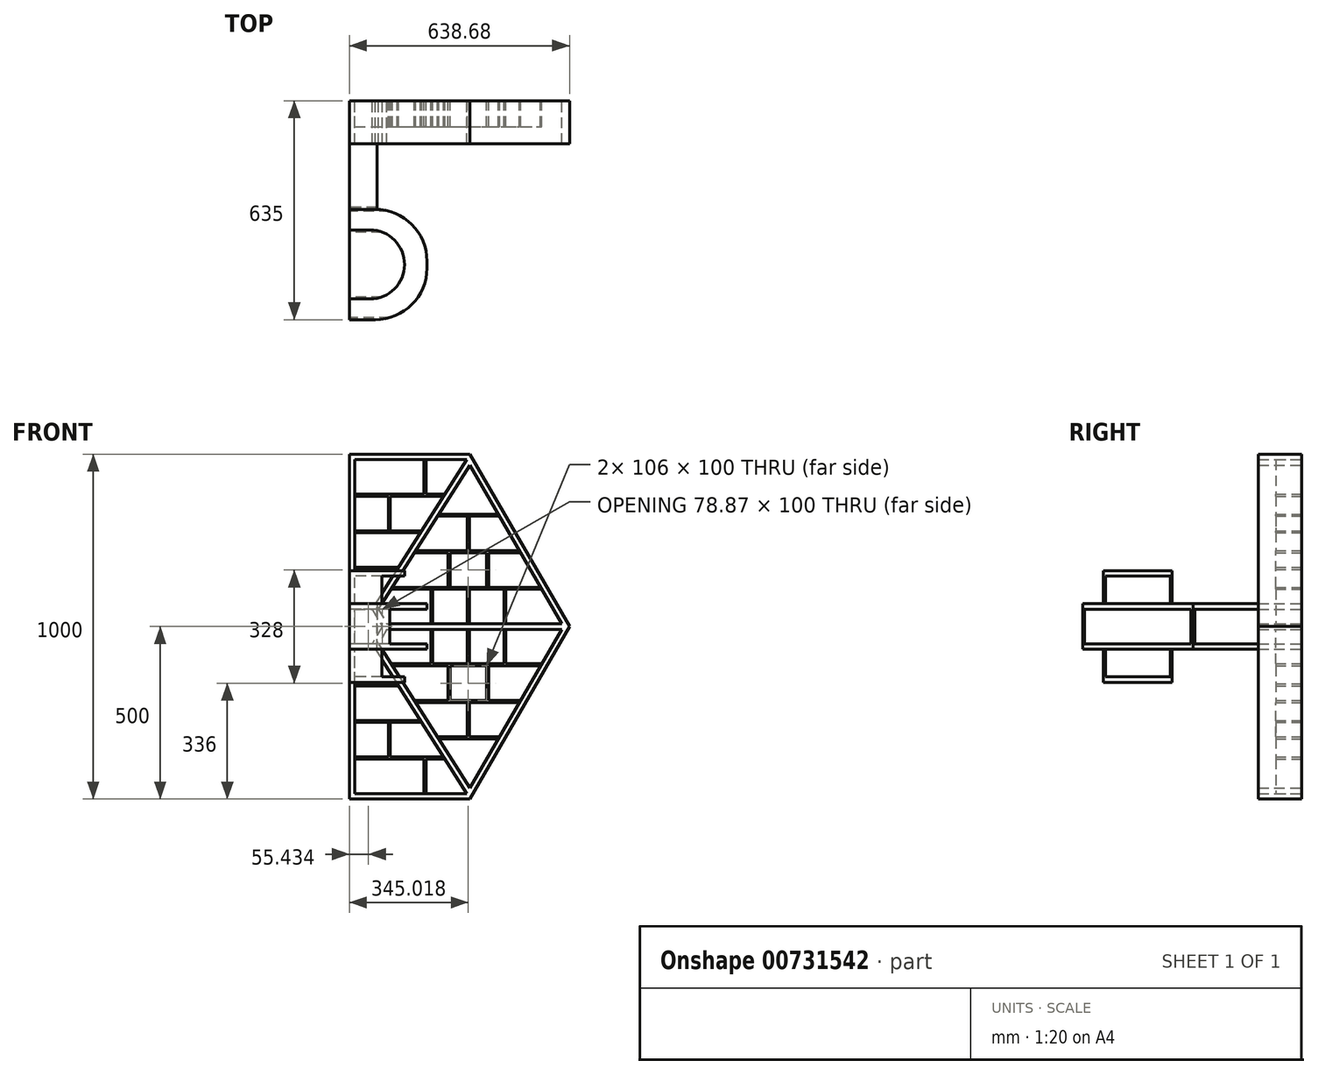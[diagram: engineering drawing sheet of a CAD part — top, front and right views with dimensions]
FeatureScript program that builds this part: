
annotation { "Feature Type Name" : "Feature", "Feature Type Description" : "" }
export const myFeature = defineFeature(function(context is Context, id is Id, definition is map)
    precondition{}
    {
        {
            var Q0;
            Q0=qCreatedBy(makeId("Front.planeOp"),FACE);
            var sketch = newSketch(context, id + "F0", { "sketchPlane" : qUnion([Q0])});
            skLineSegment(sketch, "E0", {"start": v(0, 0) * mm, "end": v(0, 1000) * mm, "construction": true});
            skLineSegment(sketch, "E1", {"start": v(0, 1000) * mm, "end": v(1200, 0) * mm, "construction": true});
            skLineSegment(sketch, "E2", {"start": v(1200, 0) * mm, "end": v(0, 0) * mm, "construction": true});
            skSolve(sketch);
        }
        {
            var Q0;
            Q0=qCreatedBy(makeId("Front.planeOp"),FACE);
            var sketch = newSketch(context, id + "F1", { "sketchPlane" : qUnion([Q0])});
            skLineSegment(sketch, "E3", {"start": v(0, 0) * mm, "end": v(350, 0) * mm});
            skLineSegment(sketch, "E4", {"start": v(350, 1000) * mm, "end": v(0, 1000) * mm});
            skLineSegment(sketch, "E5", {"start": v(0, 1000) * mm, "end": v(0, 0) * mm});
            skLineSegment(sketch, "E6", {"start": v(-31.63, 500) * mm, "end": v(1001.42, 500) * mm, "construction": true});
            skLineSegment(sketch, "E7", {"start": v(350, 1000) * mm, "end": v(638.68, 500) * mm});
            skLineSegment(sketch, "E8", {"start": v(638.68, 500) * mm, "end": v(350, 0) * mm});
            skLineSegment(sketch, "E9", {"start": v(16, 984) * mm, "end": v(340.76, 984) * mm});
            skLineSegment(sketch, "E10", {"start": v(340.76, 984) * mm, "end": v(620.2, 500) * mm});
            skLineSegment(sketch, "E11", {"start": v(620.2, 500) * mm, "end": v(340.76, 16) * mm});
            skLineSegment(sketch, "E12", {"start": v(340.76, 16) * mm, "end": v(16, 16) * mm});
            skLineSegment(sketch, "E13", {"start": v(16, 16) * mm, "end": v(16, 984) * mm});
            skLineSegment(sketch, "E14", {"start": v(16, 550) * mm, "end": v(66, 550) * mm});
            skLineSegment(sketch, "E15", {"start": v(66, 550) * mm, "end": v(94.87, 500) * mm});
            skLineSegment(sketch, "E16", {"start": v(94.87, 500) * mm, "end": v(66, 450) * mm});
            skLineSegment(sketch, "E17", {"start": v(66, 450) * mm, "end": v(16, 450) * mm});
            skLineSegment(sketch, "E18", {"start": v(16, 450) * mm, "end": v(16, 550) * mm});
            skLineSegment(sketch, "E19.0", {"start": v(75.24, 434) * mm, "end": v(16, 434) * mm});
            skLineSegment(sketch, "E19.1", {"start": v(113.34, 500) * mm, "end": v(75.24, 434) * mm});
            skLineSegment(sketch, "E19.2", {"start": v(75.24, 566) * mm, "end": v(113.34, 500) * mm});
            skLineSegment(sketch, "E19.3", {"start": v(16, 566) * mm, "end": v(75.24, 566) * mm});
            skLineSegment(sketch, "E20", {"start": v(340.76, 984) * mm, "end": v(75.24, 566) * mm});
            skLineSegment(sketch, "E21", {"start": v(75.24, 434) * mm, "end": v(340.76, 16) * mm});
            skLineSegment(sketch, "E22", {"start": v(113.34, 500) * mm, "end": v(620.2, 500) * mm, "construction": true});
            skLineSegment(sketch, "E23", {"start": v(84.26, 449.63) * mm, "end": v(349.79, 31.63) * mm});
            skLineSegment(sketch, "E24", {"start": v(84.26, 550.37) * mm, "end": v(349.79, 968.37) * mm});
            skLineSegment(sketch, "E25", {"start": v(108.72, 508) * mm, "end": v(615.58, 508) * mm});
            skLineSegment(sketch, "E26", {"start": v(108.72, 492) * mm, "end": v(615.58, 492) * mm});
            skLineSegment(sketch, "E27", {"start": v(120.87, 608) * mm, "end": v(557.85, 608) * mm});
            skLineSegment(sketch, "E28", {"start": v(124.68, 614) * mm, "end": v(554.38, 614) * mm});
            skLineSegment(sketch, "E29", {"start": v(188.2, 714) * mm, "end": v(496.65, 714) * mm});
            skLineSegment(sketch, "E30", {"start": v(192.02, 720) * mm, "end": v(493.18, 720) * mm});
            skLineSegment(sketch, "E31", {"start": v(255.54, 820) * mm, "end": v(435.45, 820) * mm});
            skLineSegment(sketch, "E32", {"start": v(259.35, 826) * mm, "end": v(431.98, 826) * mm});
            skLineSegment(sketch, "E33", {"start": v(16, 884) * mm, "end": v(277.24, 884) * mm});
            skLineSegment(sketch, "E34", {"start": v(16, 878) * mm, "end": v(273.43, 878) * mm});
            skLineSegment(sketch, "E35", {"start": v(16, 778) * mm, "end": v(209.9, 778) * mm});
            skLineSegment(sketch, "E36", {"start": v(16, 772) * mm, "end": v(206.1, 772) * mm});
            skLineSegment(sketch, "E37", {"start": v(16, 672) * mm, "end": v(142.57, 672) * mm});
            skLineSegment(sketch, "E38", {"start": v(16, 666) * mm, "end": v(138.76, 666) * mm});
            skLineSegment(sketch, "E39.MirrorCS", {"start": v(120.87, 392) * mm, "end": v(557.85, 392) * mm});
            skLineSegment(sketch, "E40.MirrorCS", {"start": v(124.68, 386) * mm, "end": v(554.38, 386) * mm});
            skLineSegment(sketch, "E41.MirrorCS", {"start": v(188.2, 286) * mm, "end": v(496.65, 286) * mm});
            skLineSegment(sketch, "E42.MirrorCS", {"start": v(192.02, 280) * mm, "end": v(493.18, 280) * mm});
            skLineSegment(sketch, "E43.MirrorCS", {"start": v(255.54, 180) * mm, "end": v(435.45, 180) * mm});
            skLineSegment(sketch, "E44.MirrorCS", {"start": v(259.35, 174) * mm, "end": v(431.98, 174) * mm});
            skLineSegment(sketch, "E45.MirrorCS", {"start": v(16, 116) * mm, "end": v(277.24, 116) * mm});
            skLineSegment(sketch, "E46.MirrorCS", {"start": v(16, 122) * mm, "end": v(273.43, 122) * mm});
            skLineSegment(sketch, "E47.MirrorCS", {"start": v(16, 222) * mm, "end": v(209.9, 222) * mm});
            skLineSegment(sketch, "E48.MirrorCS", {"start": v(16, 228) * mm, "end": v(206.1, 228) * mm});
            skLineSegment(sketch, "E49.MirrorCS", {"start": v(16, 328) * mm, "end": v(142.57, 328) * mm});
            skLineSegment(sketch, "E50.MirrorCS", {"start": v(16, 334) * mm, "end": v(138.76, 334) * mm});
            skLineSegment(sketch, "E51", {"start": v(112.95, 778) * mm, "end": v(112.95, 878) * mm});
            skLineSegment(sketch, "E52", {"start": v(118.95, 878) * mm, "end": v(118.95, 778) * mm});
            skLineSegment(sketch, "E53", {"start": v(216, 884) * mm, "end": v(216, 984) * mm});
            skLineSegment(sketch, "E54", {"start": v(222, 984) * mm, "end": v(222, 884) * mm});
            skLineSegment(sketch, "E55.MirrorCS", {"start": v(112.95, 222) * mm, "end": v(112.95, 122) * mm});
            skLineSegment(sketch, "E56.MirrorCS", {"start": v(118.95, 122) * mm, "end": v(118.95, 222) * mm});
            skLineSegment(sketch, "E57.MirrorCS", {"start": v(216, 116) * mm, "end": v(216, 16) * mm});
            skLineSegment(sketch, "E58.MirrorCS", {"start": v(222, 16) * mm, "end": v(222, 116) * mm});
            skLineSegment(sketch, "E59", {"start": v(342.02, 820) * mm, "end": v(342.02, 720) * mm});
            skLineSegment(sketch, "E60", {"start": v(348.02, 820) * mm, "end": v(348.02, 720) * mm});
            skLineSegment(sketch, "E61", {"start": v(292.02, 714) * mm, "end": v(292.02, 614) * mm});
            skLineSegment(sketch, "E62", {"start": v(286.02, 614) * mm, "end": v(292.02, 614) * mm});
            skLineSegment(sketch, "E63", {"start": v(286.02, 614) * mm, "end": v(286.02, 714) * mm});
            skLineSegment(sketch, "E64", {"start": v(404.02, 714) * mm, "end": v(404.02, 614) * mm});
            skLineSegment(sketch, "E65", {"start": v(404.02, 614) * mm, "end": v(398.02, 614) * mm});
            skLineSegment(sketch, "E66", {"start": v(398.02, 614) * mm, "end": v(398.02, 714) * mm});
            skLineSegment(sketch, "E67", {"start": v(342.02, 608) * mm, "end": v(342.02, 508) * mm});
            skLineSegment(sketch, "E68", {"start": v(342.02, 508) * mm, "end": v(348.02, 508) * mm});
            skLineSegment(sketch, "E69", {"start": v(348.02, 508) * mm, "end": v(348.02, 608) * mm});
            skLineSegment(sketch, "E70", {"start": v(448.02, 508) * mm, "end": v(448.02, 608) * mm});
            skLineSegment(sketch, "E71", {"start": v(448.02, 608) * mm, "end": v(454.02, 608) * mm});
            skLineSegment(sketch, "E72", {"start": v(454.02, 608) * mm, "end": v(454.02, 508) * mm});
            skLineSegment(sketch, "E73", {"start": v(242.02, 608) * mm, "end": v(242.02, 508) * mm});
            skLineSegment(sketch, "E74", {"start": v(236.02, 608) * mm, "end": v(236.02, 508) * mm});
            skLineSegment(sketch, "E75.MirrorCS", {"start": v(342.02, 180) * mm, "end": v(342.02, 280) * mm});
            skLineSegment(sketch, "E76.MirrorCS", {"start": v(348.02, 180) * mm, "end": v(348.02, 280) * mm});
            skLineSegment(sketch, "E77.MirrorCS", {"start": v(404.02, 286) * mm, "end": v(404.02, 386) * mm});
            skLineSegment(sketch, "E78.MirrorCS", {"start": v(398.02, 386) * mm, "end": v(398.02, 286) * mm});
            skLineSegment(sketch, "E79.MirrorCS", {"start": v(292.02, 286) * mm, "end": v(292.02, 386) * mm});
            skLineSegment(sketch, "E80.MirrorCS", {"start": v(286.02, 386) * mm, "end": v(286.02, 286) * mm});
            skLineSegment(sketch, "E81.MirrorCS", {"start": v(236.02, 392) * mm, "end": v(236.02, 492) * mm});
            skLineSegment(sketch, "E82.MirrorCS", {"start": v(242.02, 392) * mm, "end": v(242.02, 492) * mm});
            skLineSegment(sketch, "E83.MirrorCS", {"start": v(342.02, 392) * mm, "end": v(342.02, 492) * mm});
            skLineSegment(sketch, "E84.MirrorCS", {"start": v(348.02, 492) * mm, "end": v(348.02, 392) * mm});
            skLineSegment(sketch, "E85.MirrorCS", {"start": v(448.02, 492) * mm, "end": v(448.02, 392) * mm});
            skLineSegment(sketch, "E86.MirrorCS", {"start": v(454.02, 392) * mm, "end": v(454.02, 492) * mm});
            skSolve(sketch);
        }
        {
            var Q0;
            {var subQ4=sQuery(id+"F1.wireOp",EDGE,"E21");var subQ9=makeQuery(id+"F1.imprint","INTERSECT",VERTEX,{"derivedFrom":[subQ4,sQuery(id+"F1.wireOp",EDGE,"E46.MirrorCS")]});Q0=makeQuery(id+"F1.imprint","IMPRINT",FACE,{"disambiguationData":[TD([[makeQuery(id+"F1.imprint","IMPRINT",EDGE,{"disambiguationData":[TD([[subQ9,1.0]])],"derivedFrom":subQ4}),1.0]])]});}
            var Q1;
            {var subQ7=sQuery(id+"F1.wireOp",EDGE,"E14");Q1=makeQuery(id+"F1.imprint","IMPRINT",FACE,{"disambiguationData":[TD([[makeQuery(id+"F1.imprint","IMPRINT",EDGE,{"derivedFrom":subQ7}),1.0]])]});}
            var Q2;
            Q2=makeQuery(id+"F1.imprint","IMPRINT",FACE,{"disambiguationData":[TD([[makeQuery(id+"F1.imprint","IMPRINT",EDGE,{"derivedFrom":sQuery(id+"F1.wireOp",EDGE,"E3")}),1.0]])]});
            var Q3;
            {var subQ4=sQuery(id+"F1.wireOp",EDGE,"E20");var subQ5=makeQuery(id+"F1.imprint","INTERSECT",VERTEX,{"derivedFrom":[subQ4,sQuery(id+"F1.wireOp",EDGE,"E36")]});Q3=makeQuery(id+"F1.imprint","IMPRINT",FACE,{"disambiguationData":[TD([[makeQuery(id+"F1.imprint","IMPRINT",EDGE,{"disambiguationData":[TD([[subQ5,-1.0]])],"derivedFrom":subQ4}),1.0]])]});}
            var Q4;
            {var subQ3=sQuery(id+"F1.wireOp",EDGE,"E11");var subQ4=sQuery(id+"F1.wireOp",EDGE,"E10");var subQ5=makeQuery(id+"F1.imprint","INTERSECT",VERTEX,{"derivedFrom":[subQ4,subQ3]});Q4=makeQuery(id+"F1.imprint","IMPRINT",FACE,{"disambiguationData":[TD([[makeQuery(id+"F1.imprint","IMPRINT",EDGE,{"disambiguationData":[TD([[subQ5,1.0]])],"derivedFrom":subQ4}),-1.0]])]});}
            extrude(context, id + "F2", {"entities" : qUnion([Q0, Q1, Q2, Q3, Q4]), "depth" : 125 * mm, "offsetDistance" : 25 * mm});
        }
        {
            var Q0;
            {var subQ0=sQuery(id+"F1.wireOp",EDGE,"E45.MirrorCS");var subQ4=sQuery(id+"F1.wireOp",EDGE,"E13");var subQ5=makeQuery(id+"F1.imprint","INTERSECT",VERTEX,{"derivedFrom":[subQ4,subQ0]});Q0=makeQuery(id+"F1.imprint","IMPRINT",FACE,{"disambiguationData":[TD([[makeQuery(id+"F1.imprint","IMPRINT",EDGE,{"disambiguationData":[TD([[subQ5,-1.0]])],"derivedFrom":subQ4}),-1.0]])]});}
            var Q1;
            {var subQ0=sQuery(id+"F1.wireOp",EDGE,"E57.MirrorCS");Q1=makeQuery(id+"F1.imprint","IMPRINT",FACE,{"disambiguationData":[TD([[makeQuery(id+"F1.imprint","IMPRINT",EDGE,{"derivedFrom":subQ0}),1.0]])]});}
            var Q2;
            {var subQ2=sQuery(id+"F1.wireOp",EDGE,"E55.MirrorCS");Q2=makeQuery(id+"F1.imprint","IMPRINT",FACE,{"disambiguationData":[TD([[makeQuery(id+"F1.imprint","IMPRINT",EDGE,{"derivedFrom":subQ2}),1.0]])]});}
            var Q3;
            {var subQ7=sQuery(id+"F1.wireOp",EDGE,"E48.MirrorCS");Q3=makeQuery(id+"F1.imprint","IMPRINT",FACE,{"disambiguationData":[TD([[makeQuery(id+"F1.imprint","IMPRINT",EDGE,{"derivedFrom":subQ7}),-1.0]])]});}
            var Q4;
            {var subQ2=sQuery(id+"F1.wireOp",EDGE,"E49.MirrorCS");Q4=makeQuery(id+"F1.imprint","IMPRINT",FACE,{"disambiguationData":[TD([[makeQuery(id+"F1.imprint","IMPRINT",EDGE,{"derivedFrom":subQ2}),1.0]])]});}
            var Q5;
            {var subQ7=sQuery(id+"F1.wireOp",EDGE,"E44.MirrorCS");Q5=makeQuery(id+"F1.imprint","IMPRINT",FACE,{"disambiguationData":[TD([[makeQuery(id+"F1.imprint","IMPRINT",EDGE,{"derivedFrom":subQ7}),1.0]])]});}
            var Q6;
            {var subQ2=sQuery(id+"F1.wireOp",EDGE,"E75.MirrorCS");Q6=makeQuery(id+"F1.imprint","IMPRINT",FACE,{"disambiguationData":[TD([[makeQuery(id+"F1.imprint","IMPRINT",EDGE,{"derivedFrom":subQ2}),-1.0]])]});}
            var Q7;
            {var subQ6=sQuery(id+"F1.wireOp",EDGE,"E42.MirrorCS");var subQ8=sQuery(id+"F1.wireOp",EDGE,"E11");var subQ9=makeQuery(id+"F1.imprint","INTERSECT",VERTEX,{"derivedFrom":[subQ8,subQ6]});Q7=makeQuery(id+"F1.imprint","IMPRINT",FACE,{"disambiguationData":[TD([[makeQuery(id+"F1.imprint","IMPRINT",EDGE,{"disambiguationData":[TD([[subQ9,1.0]])],"derivedFrom":subQ8}),-1.0]])]});}
            var Q8;
            {var subQ0=sQuery(id+"F1.wireOp",EDGE,"E79.MirrorCS");Q8=makeQuery(id+"F1.imprint","IMPRINT",FACE,{"disambiguationData":[TD([[makeQuery(id+"F1.imprint","IMPRINT",EDGE,{"derivedFrom":subQ0}),1.0]])]});}
            var Q9;
            {var subQ0=sQuery(id+"F1.wireOp",EDGE,"E77.MirrorCS");Q9=makeQuery(id+"F1.imprint","IMPRINT",FACE,{"disambiguationData":[TD([[makeQuery(id+"F1.imprint","IMPRINT",EDGE,{"derivedFrom":subQ0}),1.0]])]});}
            var Q10;
            {var subQ0=sQuery(id+"F1.wireOp",EDGE,"E40.MirrorCS");var subQ11=sQuery(id+"F1.wireOp",EDGE,"E11");var subQ12=makeQuery(id+"F1.imprint","INTERSECT",VERTEX,{"derivedFrom":[subQ11,subQ0]});Q10=makeQuery(id+"F1.imprint","IMPRINT",FACE,{"disambiguationData":[TD([[makeQuery(id+"F1.imprint","IMPRINT",EDGE,{"disambiguationData":[TD([[subQ12,1.0]])],"derivedFrom":subQ11}),-1.0]])]});}
            var Q11;
            {var subQ2=sQuery(id+"F1.wireOp",EDGE,"E83.MirrorCS");Q11=makeQuery(id+"F1.imprint","IMPRINT",FACE,{"disambiguationData":[TD([[makeQuery(id+"F1.imprint","IMPRINT",EDGE,{"derivedFrom":subQ2}),-1.0]])]});}
            var Q12;
            {var subQ0=sQuery(id+"F1.wireOp",EDGE,"E81.MirrorCS");Q12=makeQuery(id+"F1.imprint","IMPRINT",FACE,{"disambiguationData":[TD([[makeQuery(id+"F1.imprint","IMPRINT",EDGE,{"derivedFrom":subQ0}),-1.0]])]});}
            var Q13;
            {var subQ2=sQuery(id+"F1.wireOp",EDGE,"E85.MirrorCS");Q13=makeQuery(id+"F1.imprint","IMPRINT",FACE,{"disambiguationData":[TD([[makeQuery(id+"F1.imprint","IMPRINT",EDGE,{"derivedFrom":subQ2}),1.0]])]});}
            var Q14;
            {var subQ0=sQuery(id+"F1.wireOp",EDGE,"E64");Q14=makeQuery(id+"F1.imprint","IMPRINT",FACE,{"disambiguationData":[TD([[makeQuery(id+"F1.imprint","IMPRINT",EDGE,{"derivedFrom":subQ0}),-1.0]])]});}
            var Q15;
            {var subQ0=sQuery(id+"F1.wireOp",EDGE,"E29");var subQ9=sQuery(id+"F1.wireOp",EDGE,"E10");var subQ11=makeQuery(id+"F1.imprint","INTERSECT",VERTEX,{"derivedFrom":[subQ9,subQ0]});Q15=makeQuery(id+"F1.imprint","IMPRINT",FACE,{"disambiguationData":[TD([[makeQuery(id+"F1.imprint","IMPRINT",EDGE,{"disambiguationData":[TD([[subQ11,1.0]])],"derivedFrom":subQ9}),-1.0]])]});}
            var Q16;
            {var subQ2=sQuery(id+"F1.wireOp",EDGE,"E59");Q16=makeQuery(id+"F1.imprint","IMPRINT",FACE,{"disambiguationData":[TD([[makeQuery(id+"F1.imprint","IMPRINT",EDGE,{"derivedFrom":subQ2}),1.0]])]});}
            var Q17;
            {var subQ0=sQuery(id+"F1.wireOp",EDGE,"E28");var subQ12=sQuery(id+"F1.wireOp",EDGE,"E10");var subQ13=makeQuery(id+"F1.imprint","INTERSECT",VERTEX,{"derivedFrom":[subQ12,subQ0]});Q17=makeQuery(id+"F1.imprint","IMPRINT",FACE,{"disambiguationData":[TD([[makeQuery(id+"F1.imprint","IMPRINT",EDGE,{"disambiguationData":[TD([[subQ13,-1.0]])],"derivedFrom":subQ12}),-1.0]])]});}
            var Q18;
            {var subQ2=sQuery(id+"F1.wireOp",EDGE,"E70");Q18=makeQuery(id+"F1.imprint","IMPRINT",FACE,{"disambiguationData":[TD([[makeQuery(id+"F1.imprint","IMPRINT",EDGE,{"derivedFrom":subQ2}),-1.0]])]});}
            var Q19;
            {var subQ0=sQuery(id+"F1.wireOp",EDGE,"E73");Q19=makeQuery(id+"F1.imprint","IMPRINT",FACE,{"disambiguationData":[TD([[makeQuery(id+"F1.imprint","IMPRINT",EDGE,{"derivedFrom":subQ0}),-1.0]])]});}
            var Q20;
            {var subQ2=sQuery(id+"F1.wireOp",EDGE,"E67");Q20=makeQuery(id+"F1.imprint","IMPRINT",FACE,{"disambiguationData":[TD([[makeQuery(id+"F1.imprint","IMPRINT",EDGE,{"derivedFrom":subQ2}),1.0]])]});}
            var Q21;
            {var subQ0=sQuery(id+"F1.wireOp",EDGE,"E37");Q21=makeQuery(id+"F1.imprint","IMPRINT",FACE,{"disambiguationData":[TD([[makeQuery(id+"F1.imprint","IMPRINT",EDGE,{"derivedFrom":subQ0}),-1.0]])]});}
            var Q22;
            {var subQ4=sQuery(id+"F1.wireOp",EDGE,"E36");Q22=makeQuery(id+"F1.imprint","IMPRINT",FACE,{"disambiguationData":[TD([[makeQuery(id+"F1.imprint","IMPRINT",EDGE,{"derivedFrom":subQ4}),1.0]])]});}
            var Q23;
            {var subQ2=sQuery(id+"F1.wireOp",EDGE,"E51");Q23=makeQuery(id+"F1.imprint","IMPRINT",FACE,{"disambiguationData":[TD([[makeQuery(id+"F1.imprint","IMPRINT",EDGE,{"derivedFrom":subQ2}),-1.0]])]});}
            var Q24;
            {var subQ0=sQuery(id+"F1.wireOp",EDGE,"E33");var subQ4=sQuery(id+"F1.wireOp",EDGE,"E13");var subQ5=makeQuery(id+"F1.imprint","INTERSECT",VERTEX,{"derivedFrom":[subQ4,subQ0]});Q24=makeQuery(id+"F1.imprint","IMPRINT",FACE,{"disambiguationData":[TD([[makeQuery(id+"F1.imprint","IMPRINT",EDGE,{"disambiguationData":[TD([[subQ5,1.0]])],"derivedFrom":subQ4}),-1.0]])]});}
            var Q25;
            {var subQ2=sQuery(id+"F1.wireOp",EDGE,"E53");Q25=makeQuery(id+"F1.imprint","IMPRINT",FACE,{"disambiguationData":[TD([[makeQuery(id+"F1.imprint","IMPRINT",EDGE,{"derivedFrom":subQ2}),-1.0]])]});}
            var Q26;
            {var subQ4=sQuery(id+"F1.wireOp",EDGE,"E32");Q26=makeQuery(id+"F1.imprint","IMPRINT",FACE,{"disambiguationData":[TD([[makeQuery(id+"F1.imprint","IMPRINT",EDGE,{"derivedFrom":subQ4}),-1.0]])]});}
            var Q27;
            {var subQ0=sQuery(id+"F1.wireOp",EDGE,"E61");Q27=makeQuery(id+"F1.imprint","IMPRINT",FACE,{"disambiguationData":[TD([[makeQuery(id+"F1.imprint","IMPRINT",EDGE,{"derivedFrom":subQ0}),-1.0]])]});}
            extrude(context, id + "F3", {"entities" : qUnion([Q0, Q1, Q2, Q3, Q4, Q5, Q6, Q7, Q8, Q9, Q10, Q11, Q12, Q13, Q14, Q15, Q16, Q17, Q18, Q19, Q20, Q21, Q22, Q23, Q24, Q25, Q26, Q27]), "operationType" : NewBodyOperationType.ADD, "depth" : 75 * mm, "offsetDistance" : 25 * mm});
        }
        {
            var Q0;
            Q0=qCreatedBy(makeId("Right.planeOp"),FACE);
            var sketch = newSketch(context, id + "F4", { "sketchPlane" : qUnion([Q0])});
            skLineSegment(sketch, "E87", {"start": v(0, 0) * mm, "end": v(0, 951) * mm, "construction": true});
            skLineSegment(sketch, "E88", {"start": v(-125, 0) * mm, "end": v(-125, 1000) * mm, "construction": true});
            skLineSegment(sketch, "E89", {"start": v(-125, 500) * mm, "end": v(-825, 500) * mm, "construction": true});
            skLineSegment(sketch, "E90", {"start": v(-125, 550) * mm, "end": v(-825, 550) * mm});
            skLineSegment(sketch, "E91", {"start": v(-825, 550) * mm, "end": v(-825, 450) * mm, "construction": true});
            skLineSegment(sketch, "E92", {"start": v(-825, 450) * mm, "end": v(-125, 450) * mm});
            skLineSegment(sketch, "E93", {"start": v(-125, 566) * mm, "end": v(-825, 566) * mm});
            skLineSegment(sketch, "E94", {"start": v(-825, 566) * mm, "end": v(-825, 550) * mm});
            skLineSegment(sketch, "E95", {"start": v(-475, 500) * mm, "end": v(-475, 885.02) * mm, "construction": true});
            skLineSegment(sketch, "E96", {"start": v(-575, 646) * mm, "end": v(-375, 646) * mm});
            skLineSegment(sketch, "E97", {"start": v(-575, 662) * mm, "end": v(-375, 662) * mm});
            skLineSegment(sketch, "E98", {"start": v(-575, 662) * mm, "end": v(-575, 646) * mm});
            skLineSegment(sketch, "E99", {"start": v(-375, 662) * mm, "end": v(-375, 646) * mm});
            skLineSegment(sketch, "E100", {"start": v(-575, 646) * mm, "end": v(-575, 566) * mm});
            skLineSegment(sketch, "E101", {"start": v(-569, 646) * mm, "end": v(-569, 566) * mm});
            skLineSegment(sketch, "E102", {"start": v(-375, 646) * mm, "end": v(-375, 566) * mm});
            skLineSegment(sketch, "E103", {"start": v(-381, 646) * mm, "end": v(-381, 566) * mm});
            skLineSegment(sketch, "E104", {"start": v(-125, 566) * mm, "end": v(-125, 550) * mm});
            skCircle(sketch, "E105", {"center": v(-475, 500) * mm, "radius": 173.37 * mm, "construction": true});
            skLineSegment(sketch, "E106.MirrorCS", {"start": v(-125, 450) * mm, "end": v(-825, 450) * mm});
            skLineSegment(sketch, "E107.MirrorCS", {"start": v(-125, 434) * mm, "end": v(-825, 434) * mm});
            skLineSegment(sketch, "E108.MirrorCS", {"start": v(-825, 434) * mm, "end": v(-825, 450) * mm});
            skLineSegment(sketch, "E109.MirrorCS", {"start": v(-125, 434) * mm, "end": v(-125, 450) * mm});
            skLineSegment(sketch, "E110.MirrorCS", {"start": v(-381, 354) * mm, "end": v(-381, 434) * mm});
            skLineSegment(sketch, "E111.MirrorCS", {"start": v(-375, 354) * mm, "end": v(-375, 434) * mm});
            skLineSegment(sketch, "E112.MirrorCS", {"start": v(-575, 354) * mm, "end": v(-375, 354) * mm});
            skLineSegment(sketch, "E113.MirrorCS", {"start": v(-375, 338) * mm, "end": v(-375, 354) * mm});
            skLineSegment(sketch, "E114.MirrorCS", {"start": v(-575, 338) * mm, "end": v(-375, 338) * mm});
            skLineSegment(sketch, "E115.MirrorCS", {"start": v(-575, 354) * mm, "end": v(-575, 434) * mm});
            skLineSegment(sketch, "E116.MirrorCS", {"start": v(-569, 354) * mm, "end": v(-569, 434) * mm});
            skLineSegment(sketch, "E117.MirrorCS", {"start": v(-575, 338) * mm, "end": v(-575, 354) * mm});
            skLineSegment(sketch, "E118", {"start": v(-825, 550) * mm, "end": v(-825, 450) * mm});
            skLineSegment(sketch, "E119", {"start": v(-819, 550) * mm, "end": v(-819, 450) * mm});
            skLineSegment(sketch, "E120", {"start": v(-635, 550) * mm, "end": v(-635, 450) * mm});
            skLineSegment(sketch, "E121", {"start": v(-635, 450) * mm, "end": v(-641, 450) * mm});
            skLineSegment(sketch, "E122", {"start": v(-641, 450) * mm, "end": v(-641, 550) * mm});
            skLineSegment(sketch, "E123", {"start": v(-641, 550) * mm, "end": v(-635, 550) * mm});
            skLineSegment(sketch, "E124", {"start": v(-309, 550) * mm, "end": v(-309, 450) * mm});
            skLineSegment(sketch, "E125", {"start": v(-309, 450) * mm, "end": v(-315, 450) * mm});
            skLineSegment(sketch, "E126", {"start": v(-315, 450) * mm, "end": v(-315, 550) * mm});
            skLineSegment(sketch, "E127", {"start": v(-315, 550) * mm, "end": v(-315, 566.75) * mm});
            skLineSegment(sketch, "E128", {"start": v(-635, 550) * mm, "end": v(-635, 566.75) * mm});
            skLineSegment(sketch, "E129", {"start": v(-315, 450) * mm, "end": v(-315, 433.25) * mm});
            skLineSegment(sketch, "E130", {"start": v(-635, 450) * mm, "end": v(-635, 433.25) * mm});
            skLineSegment(sketch, "E131", {"start": v(-629, 550) * mm, "end": v(-629, 450) * mm});
            skLineSegment(sketch, "E132", {"start": v(-321, 550) * mm, "end": v(-321, 450) * mm});
            skLineSegment(sketch, "E133", {"start": v(-125, 0) * mm, "end": v(-1325, 0) * mm});
            skLineSegment(sketch, "E134", {"start": v(-125, 1000) * mm, "end": v(-1325, 1000) * mm, "construction": true});
            skLineSegment(sketch, "E135", {"start": v(-1325, 1000) * mm, "end": v(-125, 0) * mm, "construction": true});
            skSolve(sketch);
        }
        {
            var Q0;
            {var subQ3=sQuery(id+"F4.wireOp",EDGE,"kH1EobTy-9VdN-fPPy-B3AQ-T8eU9FerqOdl");Q0=makeQuery(id+"F4.imprint","IMPRINT",FACE,{"disambiguationData":[TD([[makeQuery(id+"F4.imprint","IMPRINT",EDGE,{"derivedFrom":subQ3}),-1.0]])]});}
            var Q1;
            Q1=makeQuery(id+"F4.imprint","IMPRINT",FACE,{"disambiguationData":[TD([[makeQuery(id+"F4.imprint","IMPRINT",EDGE,{"derivedFrom":sQuery(id+"F4.wireOp",EDGE,"E97")}),-1.0]])]});
            var Q2;
            {var subQ0=sQuery(id+"F4.wireOp",EDGE,"E100");Q2=makeQuery(id+"F4.imprint","IMPRINT",FACE,{"disambiguationData":[TD([[makeQuery(id+"F4.imprint","IMPRINT",EDGE,{"derivedFrom":subQ0}),1.0]])]});}
            var Q3;
            {var subQ0=sQuery(id+"F4.wireOp",EDGE,"E102");Q3=makeQuery(id+"F4.imprint","IMPRINT",FACE,{"disambiguationData":[TD([[makeQuery(id+"F4.imprint","IMPRINT",EDGE,{"derivedFrom":subQ0}),-1.0]])]});}
            var Q4;
            {var subQ4=sQuery(id+"F4.wireOp",EDGE,"JSTGoZBT-KipA-OvFC-O3C1-DViTUQ1MoIjg");Q4=makeQuery(id+"F4.imprint","IMPRINT",FACE,{"disambiguationData":[TD([[makeQuery(id+"F4.imprint","IMPRINT",EDGE,{"derivedFrom":subQ4}),-1.0]])]});}
            var Q5;
            {var subQ0=sQuery(id+"F4.wireOp",EDGE,"E113.MirrorCS");Q5=makeQuery(id+"F4.imprint","IMPRINT",FACE,{"disambiguationData":[TD([[makeQuery(id+"F4.imprint","IMPRINT",EDGE,{"derivedFrom":subQ0}),1.0]])]});}
            var Q6;
            {var subQ0=sQuery(id+"F4.wireOp",EDGE,"E110.MirrorCS");Q6=makeQuery(id+"F4.imprint","IMPRINT",FACE,{"disambiguationData":[TD([[makeQuery(id+"F4.imprint","IMPRINT",EDGE,{"derivedFrom":subQ0}),-1.0]])]});}
            var Q7;
            {var subQ0=sQuery(id+"F4.wireOp",EDGE,"E115.MirrorCS");Q7=makeQuery(id+"F4.imprint","IMPRINT",FACE,{"disambiguationData":[TD([[makeQuery(id+"F4.imprint","IMPRINT",EDGE,{"derivedFrom":subQ0}),-1.0]])]});}
            extrude(context, id + "F5", {"entities" : qUnion([Q0, Q1, Q2, Q3, Q4, Q5, Q6, Q7]), "depth" : 160 * mm, "offsetDistance" : 25 * mm});
        }
        {
            var Q0;
            {var subQ2=sQuery(id+"F4.wireOp",EDGE,"E124");Q0=makeQuery(id+"F4.imprint","IMPRINT",FACE,{"disambiguationData":[TD([[makeQuery(id+"F4.imprint","IMPRINT",EDGE,{"derivedFrom":subQ2}),-1.0]])]});}
            var Q1;
            {var subQ0=sQuery(id+"F4.wireOp",EDGE,"E104");Q1=makeQuery(id+"F4.imprint","IMPRINT",FACE,{"disambiguationData":[TD([[makeQuery(id+"F4.imprint","IMPRINT",EDGE,{"derivedFrom":subQ0}),-1.0]])]});}
            var Q2;
            {var subQ0=sQuery(id+"F4.wireOp",EDGE,"E109.MirrorCS");Q2=makeQuery(id+"F4.imprint","IMPRINT",FACE,{"disambiguationData":[TD([[makeQuery(id+"F4.imprint","IMPRINT",EDGE,{"derivedFrom":subQ0}),1.0]])]});}
            extrude(context, id + "F6", {"entities" : qUnion([Q0, Q1, Q2]), "depth" : 80 * mm, "offsetDistance" : 25 * mm});
        }
        {
            var Q0;
            Q0=makeQuery(id+"F5.opExtrude","CAP_EDGE",EDGE,{"disambiguationData":[OSD([sQuery(id+"F4.wireOp",EDGE,"E99"),sQuery(id+"F4.wireOp",EDGE,"E102")])],"isStart":false});
            var Q1;
            Q1=makeQuery(id+"F5.opExtrude","CAP_EDGE",EDGE,{"disambiguationData":[OSD([sQuery(id+"F4.wireOp",EDGE,"E111.MirrorCS"),sQuery(id+"F4.wireOp",EDGE,"E113.MirrorCS")])],"isStart":false});
            var Q2;
            Q2=makeQuery(id+"F5.opExtrude","CAP_EDGE",EDGE,{"disambiguationData":[OSD([sQuery(id+"F4.wireOp",EDGE,"E98"),sQuery(id+"F4.wireOp",EDGE,"E100")])],"isStart":false});
            var Q3;
            Q3=makeQuery(id+"F5.opExtrude","CAP_EDGE",EDGE,{"disambiguationData":[OSD([sQuery(id+"F4.wireOp",EDGE,"E115.MirrorCS"),sQuery(id+"F4.wireOp",EDGE,"E117.MirrorCS")])],"isStart":false});
            fillet(context, id + "F7", {"entities" : qUnion([Q0, Q1, Q2, Q3]), "radius" : 100 * mm, "tangentPropagation" : true, "allowEdgeOverflow" : false});
        }
        {
            var Q0;
            {var subQ4=sQuery(id+"F4.wireOp",EDGE,"E90");var subQ7=makeQuery(id+"F4.imprint","INTERSECT",VERTEX,{"derivedFrom":[subQ4,sQuery(id+"F4.wireOp",EDGE,"E132")]});Q0=makeQuery(id+"F4.imprint","IMPRINT",FACE,{"disambiguationData":[TD([[makeQuery(id+"F4.imprint","IMPRINT",EDGE,{"disambiguationData":[TD([[subQ7,-1.0]])],"derivedFrom":subQ4}),-1.0]])]});}
            var Q1;
            {var subQ0=sQuery(id+"F4.wireOp",EDGE,"E120");Q1=makeQuery(id+"F4.imprint","IMPRINT",FACE,{"disambiguationData":[TD([[makeQuery(id+"F4.imprint","IMPRINT",EDGE,{"derivedFrom":subQ0}),1.0]])]});}
            var Q2;
            {var subQ0=sQuery(id+"F4.wireOp",EDGE,"E92");var subQ1=makeQuery(id+"F4.imprint","INTERSECT",VERTEX,{"derivedFrom":[subQ0,sQuery(id+"F4.wireOp",EDGE,"E131")]});Q2=makeQuery(id+"F4.imprint","IMPRINT",FACE,{"disambiguationData":[TD([[makeQuery(id+"F4.imprint","IMPRINT",EDGE,{"disambiguationData":[TD([[subQ1,-1.0]])],"derivedFrom":subQ0}),-1.0]])]});}
            var Q3;
            {var subQ2=sQuery(id+"F4.wireOp",EDGE,"E126");Q3=makeQuery(id+"F4.imprint","IMPRINT",FACE,{"disambiguationData":[TD([[makeQuery(id+"F4.imprint","IMPRINT",EDGE,{"derivedFrom":subQ2}),1.0]])]});}
            extrude(context, id + "F8", {"entities" : qUnion([Q0, Q1, Q2, Q3]), "depth" : 225 * mm, "offsetDistance" : 25 * mm});
        }
        {
            var Q0;
            Q0=makeQuery(id+"F8.opExtrude","CAP_EDGE",EDGE,{"disambiguationData":[OSD([sQuery(id+"F4.wireOp",EDGE,"E120"),sQuery(id+"F4.wireOp",EDGE,"E128"),sQuery(id+"F4.wireOp",EDGE,"E130")])],"isStart":false});
            var Q1;
            Q1=makeQuery(id+"F8.opExtrude","CAP_EDGE",EDGE,{"disambiguationData":[OSD([sQuery(id+"F4.wireOp",EDGE,"E126"),sQuery(id+"F4.wireOp",EDGE,"E127"),sQuery(id+"F4.wireOp",EDGE,"E129")])],"isStart":false});
            fillet(context, id + "F9", {"entities" : qUnion([Q0, Q1]), "radius" : 150 * mm, "tangentPropagation" : true, "allowEdgeOverflow" : false});
        }
    });
